# Revit family: M_FF109 Pipe Fire Sleeve
name_source: partatom
category: Specialty Equipment
revit_build: Autodesk Revit 2015 (Build: 20160512_0715(x64)
units: mm (PartAtom-declared; Revit-internal decimal feet)

## types (38) — shared parameters
IFC Classification = Building Element Proxy
Manufacturer = Tenmat ltd
Material = Intumescent Sealant
Performance = BS EN 1366-3:2009 & BS 476, ETA-12/0332, 1224-CPR-0341, CE Marked
URL = https://www.tenmat.com
Youtube clip = https://www.youtube.com

## per-type parameters (varying)
| type | Connector | Description | ID | Length | OD | Pipe Material Suitability | Tenmat Item Number |
| FF109 Pipe Fire Sleeve - 17mm (200mm) | 17 mm | FireFly 109 Fire Sleeve for 17mm pipe - 200mm Length | 9 mm  [stored 0.0295276 ft] | 200 mm | 34 mm | HDEP, UPVC, PVC, Steel and Copper | I109BT00170067020000 |
| FF109 Pipe Fire Sleeve - 17mm (300mm) | 17 mm | FireFly 109 Fire Sleeve for 17mm pipe - 300mm Length | 9 mm  [stored 0.0295276 ft] | 300 mm | 34 mm | HDEP, UPVC, PVC, Steel and Copper | I109BT00170067030000 |
| FF109 Pipe Fire Sleeve - 21mm (200mm) | 21 mm  [stored 0.0688976 ft] | FireFly 109 Fire Sleeve for 21mm pipe - 200mm Length | 11 mm | 200 mm | 36 mm | HDEP, UPVC, PVC, Steel and Copper | I109BT00210071020000 |
| FF109 Pipe Fire Sleeve - 21mm (300mm) | 17 mm | FireFly 109 Fire Sleeve for 21mm pipe - 300mm Length | 9 mm  [stored 0.0295276 ft] | 300 mm | 34 mm | HDEP, UPVC, PVC, Steel and Copper | I109BT00210071030000 |
| FF109 Pipe Fire Sleeve - 27mm (200mm) | 27 mm  [stored 0.0885827 ft] | FireFly 109 Fire Sleeve for 27mm pipe - 200mm Length | 14 mm  [stored 0.0459318 ft] | 200 mm | 39 mm | HDEP, UPVC, PVC, Steel and Copper | I109BT00270077020000 |
| FF109 Pipe Fire Sleeve - 27mm (300mm) | 27 mm  [stored 0.0885827 ft] | FireFly 109 Fire Sleeve for 27mm pipe - 300mm Length | 14 mm  [stored 0.0459318 ft] | 300 mm | 39 mm | HDEP, UPVC, PVC, Steel and Copper | I109BT00270077030000 |
| FF109 Pipe Fire Sleeve - 34mm (200mm) | 34 mm | FireFly 109 Fire Sleeve for 34mm pipe - 200mm Length | 17 mm | 200 mm | 42 mm  [stored 0.137795 ft] | HDEP, UPVC, PVC, Steel and Copper | I109BT00340084020000 |
| FF109 Pipe Fire Sleeve - 34mm (300mm) | 34 mm | FireFly 109 Fire Sleeve for 34mm pipe - 300mm Length | 17 mm | 300 mm | 42 mm  [stored 0.137795 ft] | HDEP, UPVC, PVC, Steel and Copper | I109BT00340084030000 |
| FF109 Pipe Fire Sleeve - 42mm (200mm) | 42 mm  [stored 0.137795 ft] | FireFly 109 Fire Sleeve for 42mm pipe - 200mm Length | 21 mm  [stored 0.0688976 ft] | 200 mm | 46 mm  [stored 0.150919 ft] | HDEP, UPVC, PVC, Steel and Copper | I109BT00420092020000 |
| FF109 Pipe Fire Sleeve - 42mm (300mm) | 42 mm  [stored 0.137795 ft] | FireFly 109 Fire Sleeve for 42mm pipe - 300mm Length | 21 mm  [stored 0.0688976 ft] | 300 mm | 46 mm  [stored 0.150919 ft] | HDEP, UPVC, PVC, Steel and Copper | I109BT00420092030000 |
| FF109 Pipe Fire Sleeve - 48mm (200mm) | 48 mm  [stored 0.15748 ft] | FireFly 109 Fire Sleeve for 48mm pipe - 200mm Length | 24 mm  [stored 0.0787402 ft] | 200 mm | 49 mm  [stored 0.160761 ft] | HDEP, UPVC, PVC, Steel and Copper | I109BT00480098020000 |
| FF109 Pipe Fire Sleeve - 48mm (300mm) | 48 mm  [stored 0.15748 ft] | FireFly 109 Fire Sleeve for 48mm pipe - 300mm Length | 24 mm  [stored 0.0787402 ft] | 300 mm | 49 mm  [stored 0.160761 ft] | HDEP, UPVC, PVC, Steel and Copper | I109BT00480098030000 |
| FF109 Pipe Fire Sleeve - 54mm (200mm) | 54 mm  [stored 0.177165 ft] | FireFly 109 Fire Sleeve for 54mm pipe - 200mm Length | 27 mm  [stored 0.0885827 ft] | 200 mm | 52 mm | HDEP, UPVC, PVC, Steel and Copper | I109BT00540104020000 |
| FF109 Pipe Fire Sleeve - 54mm (300mm) | 54 mm  [stored 0.177165 ft] | FireFly 109 Fire Sleeve for 54mm pipe - 300mm Length | 27 mm  [stored 0.0885827 ft] | 300 mm | 52 mm | HDEP, UPVC, PVC, Steel and Copper | I109BT00540104030000 |
| FF109 Pipe Fire Sleeve - 60mm (200mm) | 60 mm  [stored 0.19685 ft] | FireFly 109 Fire Sleeve for 60mm pipe - 200mm Length | 30 mm  [stored 0.0984252 ft] | 200 mm | 55 mm  [stored 0.180446 ft] | HDEP, UPVC, PVC, Steel and Copper | I109BT00600110020000 |
| FF109 Pipe Fire Sleeve - 60mm (300mm) | 60 mm  [stored 0.19685 ft] | FireFly 109 Fire Sleeve for 60mm pipe - 300mm Length | 30 mm  [stored 0.0984252 ft] | 300 mm | 55 mm  [stored 0.180446 ft] | HDEP, UPVC, PVC, Steel and Copper | I109BT00600110030000 |
| FF109 Pipe Fire Sleeve - 67mm (200mm) | 67 mm | FireFly 109 Fire Sleeve for 67mm pipe - 200mm Length | 34 mm | 200 mm | 59 mm | HDEP, UPVC, PVC, Steel and Copper | I109BT00670117020000 |
| FF109 Pipe Fire Sleeve - 67mm (300mm) | 67 mm | FireFly 109 Fire Sleeve for 67mm pipe - 300mm Length | 34 mm | 300 mm | 59 mm | HDEP, UPVC, PVC, Steel and Copper | I109BT00670117030000 |
| FF109 Pipe Fire Sleeve - 76mm (200mm) | 152 mm | FireFly 109 Fire Sleeve for 76mm pipe - 200mm Length | 76 mm  [stored 0.249344 ft] | 200 mm | 101 mm  [stored 0.331365 ft] | HDEP, UPVC, PVC, Steel and Copper | I109BT00760126020000 |
| FF109 Pipe Fire Sleeve - 76mm (300mm) | 76 mm  [stored 0.249344 ft] | FireFly 109 Fire Sleeve for 76mm pipe - 300mm Length | 38 mm  [stored 0.124672 ft] | 300 mm | 63 mm  [stored 0.206693 ft] | HDEP, UPVC, PVC, Steel and Copper | I109BT00760126030000 |
| FF109 Pipe Fire Sleeve - 80mm (200mm) | 80 mm  [stored 0.262467 ft] | FireFly 109 Fire Sleeve for 80mm pipe - 200mm Length | 40 mm  [stored 0.131234 ft] | 200 mm | 65 mm  [stored 0.213255 ft] | HDEP, UPVC, PVC, Steel and Copper | I109BT00800130020000 |
| FF109 Pipe Fire Sleeve - 80mm (300mm) | 40 mm  [stored 0.131234 ft] | FireFly 109 Fire Sleeve for 80mm pipe - 300mm Length | 20 mm  [stored 0.0656168 ft] | 300 mm | 45 mm | HDEP, UPVC, PVC, Steel and Copper | I109BT00800130030000 |
| FF109 Pipe Fire Sleeve - 89mm (200mm) | 89 mm  [stored 0.291995 ft] | FireFly 109 Fire Sleeve for 89mm pipe - 200mm Length | 45 mm | 200 mm | 70 mm  [stored 0.229659 ft] | HDEP, UPVC, PVC, Steel and Copper | I109BT00890139020000 |
| FF109 Pipe Fire Sleeve - 89mm (300mm) | 89 mm  [stored 0.291995 ft] | FireFly 109 Fire Sleeve for 89mm pipe - 300mm Length | 45 mm | 300 mm | 70 mm  [stored 0.229659 ft] | HDEP, UPVC, PVC, Steel and Copper | I109BT00890139030000 |
| FF109 Pipe Fire Sleeve - 102mm (200mm) | 102 mm | FireFly 109 Fire Sleeve for 102mm pipe - 200mm Length | 51 mm | 200 mm | 76 mm  [stored 0.249344 ft] | HDEP, UPVC, PVC, Steel and Copper | I109BT01020152020000 |
| FF109 Pipe Fire Sleeve - 102mm (300mm) | 102 mm | FireFly 109 Fire Sleeve for 102mm pipe - 300mm Length | 51 mm | 300 mm | 76 mm  [stored 0.249344 ft] | HDEP, UPVC, PVC, Steel and Copper | I109BT01020152030000 |
| FF109 Pipe Fire Sleeve - 108mm (200mm) | 108 mm | FireFly 109 Fire Sleeve for 108mm pipe - 200mm Length | 54 mm  [stored 0.177165 ft] | 200 mm | 79 mm | HDEP, UPVC, PVC, Steel and Copper | I109BT01080158020000 |
| FF109 Pipe Fire Sleeve - 108mm (300mm) | 108 mm | FireFly 109 Fire Sleeve for 108mm pipe - 300mm Length | 54 mm  [stored 0.177165 ft] | 300 mm | 79 mm |  | I109BT01080158030000 |
| FF109 Pipe Fire Sleeve - 114mm (200mm) | 114 mm | FireFly 109 Fire Sleeve for 114mm pipe - 200mm Length | 57 mm  [stored 0.187008 ft] | 200 mm | 82 mm  [stored 0.269029 ft] | HDEP, UPVC, PVC, Steel and Copper | I109BT01140164020000 |
| FF109 Pipe Fire Sleeve - 114mm (300mm) | 114 mm | FireFly 109 Fire Sleeve for 114mm pipe - 300mm Length | 57 mm  [stored 0.187008 ft] | 300 mm | 82 mm  [stored 0.269029 ft] | HDEP, UPVC, PVC, Steel and Copper | I109BT01140164030000 |
| FF109 Pipe Fire Sleeve - 127mm (200mm) | 127 mm | FireFly 109 Fire Sleeve for 127mm pipe - 200mm Length | 64 mm | 200 mm | 89 mm  [stored 0.291995 ft] | HDEP, UPVC, PVC, Steel and Copper | I109BT01270177020000 |
| FF109 Pipe Fire Sleeve - 127mm (300mm) | 127 mm | FireFly 109 Fire Sleeve for 127mm pipe - 300mm Length | 64 mm | 300 mm | 89 mm  [stored 0.291995 ft] | HDEP, UPVC, PVC, Steel and Copper | I109BT01270177030000 |
| FF109 Pipe Fire Sleeve - 140mm (200mm) | 140 mm | FireFly 109 Fire Sleeve for 140mm pipe - 200mm Length | 70 mm  [stored 0.229659 ft] | 200 mm | 95 mm  [stored 0.31168 ft] | HDEP, UPVC, PVC, Steel and Copper | I109BT01400190020000 |
| FF109 Pipe Fire Sleeve - 140mm (300mm) | 140 mm | FireFly 109 Fire Sleeve for 140mm pipe - 300mm Length | 70 mm  [stored 0.229659 ft] | 300 mm | 95 mm  [stored 0.31168 ft] | HDEP, UPVC, PVC, Steel and Copper | I109BT01400190030000 |
| FF109 Pipe Fire Sleeve - 159mm (200mm) | 159 mm | FireFly 109 Fire Sleeve for 159mm pipe - 200mm Length | 80 mm  [stored 0.262467 ft] | 200 mm | 105 mm | HDEP, UPVC, PVC, Steel and Copper | I109BT01590209020000 |
| FF109 Pipe Fire Sleeve - 159mm (300mm) | 159 mm | FireFly 109 Fire Sleeve for 159mm pipe - 300mm Length | 80 mm  [stored 0.262467 ft] | 300 mm | 105 mm | HDEP, UPVC, PVC, Steel and Copper | I109BT01590209030000 |
| FF109 Pipe Fire Sleeve - 169mm (200mm) | 169 mm | FireFly 109 Fire Sleeve for 169mm pipe - 200mm Length | 85 mm | 200 mm | 110 mm | HDEP, UPVC, PVC, Steel and Copper | I109BT01690219020000 |
| FF109 Pipe Fire Sleeve - 169mm (300mm) | 169 mm | FireFly 109 Fire Sleeve for 169mm pipe - 300mm Length | 85 mm | 300 mm | 110 mm | HDEP, UPVC, PVC, Steel and Copper | I109BT01690219020000 |

note: [stored X ft] marks values corroborated as IEEE doubles in the binary element streams (Revit-internal decimal feet)

## geometry (parser evidence)
native form markers: Blend x2, Sweep x3
no freeform markers — native parametric forms only
